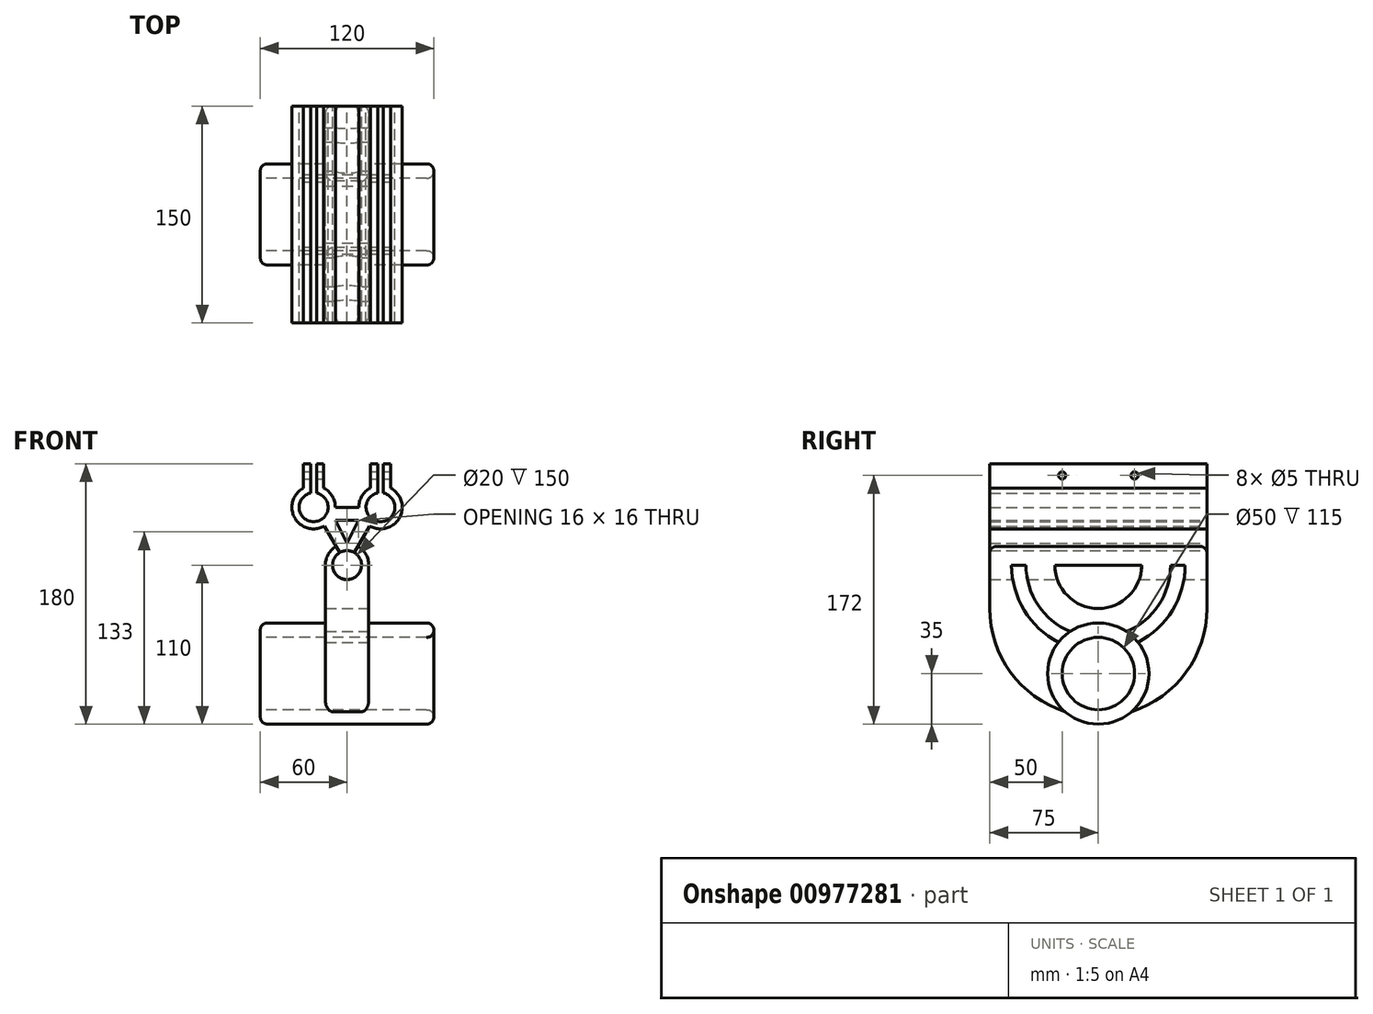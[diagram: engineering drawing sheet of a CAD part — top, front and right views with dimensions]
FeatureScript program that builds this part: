
annotation { "Feature Type Name" : "Feature", "Feature Type Description" : "" }
export const myFeature = defineFeature(function(context is Context, id is Id, definition is map)
    precondition{}
    {
        {
            var Q0;
            Q0=qCreatedBy(makeId("Front.planeOp"),FACE);
            var sketch = newSketch(context, id + "F0", { "sketchPlane" : qUnion([Q0])});
            skCircle(sketch, "E0", {"center": v(0, 0) * mm, "radius": 10 * mm});
            skCircle(sketch, "E1", {"center": v(23.1, 40) * mm, "radius": 10 * mm});
            skCircle(sketch, "E2", {"center": v(-23.1, 40) * mm, "radius": 10 * mm});
            skCircle(sketch, "E3", {"center": v(-23.1, 40) * mm, "radius": 15 * mm});
            skCircle(sketch, "E4", {"center": v(23.1, 40) * mm, "radius": 15 * mm});
            skCircle(sketch, "E5", {"center": v(0, 0) * mm, "radius": 15 * mm});
            skLineSegment(sketch, "E6", {"start": v(0, 0) * mm, "end": v(-23.1, 40) * mm});
            skLineSegment(sketch, "E7", {"start": v(23.1, 40) * mm, "end": v(0, 0) * mm});
            skLineSegment(sketch, "E8", {"start": v(-23.1, 40) * mm, "end": v(23.1, 40) * mm});
            skLineSegment(sketch, "E9.bottom", {"start": v(-2.5, 0) * mm, "end": v(2.5, 0) * mm});
            skLineSegment(sketch, "E9.top", {"start": v(-2.5, -30) * mm, "end": v(2.5, -30) * mm});
            skLineSegment(sketch, "E9.left", {"start": v(-2.5, 0) * mm, "end": v(-2.5, -30) * mm});
            skLineSegment(sketch, "E9.right", {"start": v(2.5, 0) * mm, "end": v(2.5, -30) * mm});
            skPoint(sketch, "E9.middle", {"position": v(0, -15) * mm});
            skLineSegment(sketch, "E10.bottom", {"start": v(15, -30) * mm, "end": v(-15, -30) * mm});
            skLineSegment(sketch, "E10.top", {"start": v(15, 0) * mm, "end": v(-15, 0) * mm});
            skLineSegment(sketch, "E10.left", {"start": v(15, -30) * mm, "end": v(15, 0) * mm});
            skLineSegment(sketch, "E10.right", {"start": v(-15, -30) * mm, "end": v(-15, 0) * mm});
            skPoint(sketch, "E11.middle", {"position": v(0, 40) * mm});
            skLineSegment(sketch, "E12.bottom", {"start": v(30.1, 70) * mm, "end": v(16.1, 70) * mm});
            skLineSegment(sketch, "E12.top", {"start": v(30.1, 40) * mm, "end": v(16.1, 40) * mm});
            skLineSegment(sketch, "E12.left", {"start": v(30.1, 70) * mm, "end": v(30.1, 40) * mm});
            skLineSegment(sketch, "E12.right", {"start": v(16.1, 70) * mm, "end": v(16.1, 40) * mm});
            skPoint(sketch, "E12.middle", {"position": v(23.1, 55) * mm});
            skLineSegment(sketch, "E13.bottom", {"start": v(-16.1, 70) * mm, "end": v(-30.1, 70) * mm});
            skLineSegment(sketch, "E13.top", {"start": v(-16.1, 40) * mm, "end": v(-30.1, 40) * mm});
            skLineSegment(sketch, "E13.left", {"start": v(-16.1, 70) * mm, "end": v(-16.1, 40) * mm});
            skLineSegment(sketch, "E13.right", {"start": v(-30.1, 70) * mm, "end": v(-30.1, 40) * mm});
            skPoint(sketch, "E13.middle", {"position": v(-23.1, 55) * mm});
            skLineSegment(sketch, "E14.bottom", {"start": v(-25.1, 70) * mm, "end": v(-21.1, 70) * mm});
            skLineSegment(sketch, "E14.top", {"start": v(-25.1, 40) * mm, "end": v(-21.1, 40) * mm});
            skLineSegment(sketch, "E14.left", {"start": v(-25.1, 70) * mm, "end": v(-25.1, 40) * mm});
            skLineSegment(sketch, "E14.right", {"start": v(-21.1, 70) * mm, "end": v(-21.1, 40) * mm});
            skLineSegment(sketch, "E15.bottom", {"start": v(21.1, 70) * mm, "end": v(25.1, 70) * mm});
            skLineSegment(sketch, "E15.top", {"start": v(21.1, 40) * mm, "end": v(25.1, 40) * mm});
            skLineSegment(sketch, "E15.left", {"start": v(21.1, 70) * mm, "end": v(21.1, 40) * mm});
            skLineSegment(sketch, "E15.right", {"start": v(25.1, 70) * mm, "end": v(25.1, 40) * mm});
            skSolve(sketch);
        }
        {
            var Q0;
            {var subQ0=sQuery(id+"F0.wireOp",EDGE,"E13.left");var subQ1=sQuery(id+"F0.wireOp",EDGE,"E3");var subQ2=makeQuery(id+"F0.imprint","INTERSECT",VERTEX,{"derivedFrom":[subQ1,subQ0]});Q0=makeQuery(id+"F0.imprint","IMPRINT",FACE,{"disambiguationData":[TD([[makeQuery(id+"F0.imprint","IMPRINT",EDGE,{"disambiguationData":[TD([[subQ2,-1.0]])],"derivedFrom":subQ1}),-1.0]])]});}
            var Q1;
            {var subQ0=sQuery(id+"F0.wireOp",EDGE,"E13.right");var subQ1=sQuery(id+"F0.wireOp",EDGE,"E3");var subQ2=makeQuery(id+"F0.imprint","INTERSECT",VERTEX,{"derivedFrom":[subQ1,subQ0]});Q1=makeQuery(id+"F0.imprint","IMPRINT",FACE,{"disambiguationData":[TD([[makeQuery(id+"F0.imprint","IMPRINT",EDGE,{"disambiguationData":[TD([[subQ2,1.0]])],"derivedFrom":subQ1}),-1.0]])]});}
            var Q2;
            {var subQ0=sQuery(id+"F0.wireOp",EDGE,"E12.left");var subQ1=sQuery(id+"F0.wireOp",EDGE,"E4");var subQ2=makeQuery(id+"F0.imprint","INTERSECT",VERTEX,{"derivedFrom":[subQ1,subQ0]});Q2=makeQuery(id+"F0.imprint","IMPRINT",FACE,{"disambiguationData":[TD([[makeQuery(id+"F0.imprint","IMPRINT",EDGE,{"disambiguationData":[TD([[subQ2,-1.0]])],"derivedFrom":subQ1}),-1.0]])]});}
            var Q3;
            {var subQ0=sQuery(id+"F0.wireOp",EDGE,"E12.right");var subQ1=sQuery(id+"F0.wireOp",EDGE,"E4");var subQ2=makeQuery(id+"F0.imprint","INTERSECT",VERTEX,{"derivedFrom":[subQ1,subQ0]});Q3=makeQuery(id+"F0.imprint","IMPRINT",FACE,{"disambiguationData":[TD([[makeQuery(id+"F0.imprint","IMPRINT",EDGE,{"disambiguationData":[TD([[subQ2,1.0]])],"derivedFrom":subQ1}),-1.0]])]});}
            var Q4;
            {var subQ0=sQuery(id+"F0.wireOp",EDGE,"E10.right");var subQ1=sQuery(id+"F0.wireOp",EDGE,"E5");var subQ2=makeQuery(id+"F0.imprint","INTERSECT",VERTEX,{"derivedFrom":[subQ1,subQ0]});Q4=makeQuery(id+"F0.imprint","IMPRINT",FACE,{"disambiguationData":[TD([[makeQuery(id+"F0.imprint","IMPRINT",EDGE,{"disambiguationData":[TD([[subQ2,-1.0]])],"derivedFrom":subQ1}),-1.0]])]});}
            var Q5;
            {var subQ0=sQuery(id+"F0.wireOp",EDGE,"E10.left");var subQ1=sQuery(id+"F0.wireOp",EDGE,"E5");var subQ2=makeQuery(id+"F0.imprint","INTERSECT",VERTEX,{"derivedFrom":[subQ1,subQ0]});Q5=makeQuery(id+"F0.imprint","IMPRINT",FACE,{"disambiguationData":[TD([[makeQuery(id+"F0.imprint","IMPRINT",EDGE,{"disambiguationData":[TD([[subQ2,1.0]])],"derivedFrom":subQ1}),-1.0]])]});}
            var Q6;
            {var subQ0=sQuery(id+"F0.wireOp",EDGE,"E6");var subQ1=sQuery(id+"F0.wireOp",EDGE,"E0");var subQ2=makeQuery(id+"F0.imprint","INTERSECT",VERTEX,{"derivedFrom":[subQ1,subQ0]});Q6=makeQuery(id+"F0.imprint","IMPRINT",FACE,{"disambiguationData":[TD([[makeQuery(id+"F0.imprint","IMPRINT",EDGE,{"disambiguationData":[TD([[subQ2,-1.0]])],"derivedFrom":subQ1}),-1.0]])]});}
            var Q7;
            {var subQ0=sQuery(id+"F0.wireOp",EDGE,"E7");var subQ1=sQuery(id+"F0.wireOp",EDGE,"E0");var subQ2=makeQuery(id+"F0.imprint","INTERSECT",VERTEX,{"derivedFrom":[subQ1,subQ0]});Q7=makeQuery(id+"F0.imprint","IMPRINT",FACE,{"disambiguationData":[TD([[makeQuery(id+"F0.imprint","IMPRINT",EDGE,{"disambiguationData":[TD([[subQ2,1.0]])],"derivedFrom":subQ1}),-1.0]])]});}
            var Q8;
            {var subQ0=sQuery(id+"F0.wireOp",EDGE,"E12.right");var subQ1=sQuery(id+"F0.wireOp",EDGE,"E1");var subQ2=makeQuery(id+"F0.imprint","INTERSECT",VERTEX,{"derivedFrom":[subQ1,subQ0]});Q8=makeQuery(id+"F0.imprint","IMPRINT",FACE,{"disambiguationData":[TD([[makeQuery(id+"F0.imprint","IMPRINT",EDGE,{"disambiguationData":[TD([[subQ2,-1.0]])],"derivedFrom":subQ1}),-1.0]])]});}
            var Q9;
            {var subQ0=sQuery(id+"F0.wireOp",EDGE,"E12.left");var subQ1=sQuery(id+"F0.wireOp",EDGE,"E1");var subQ2=makeQuery(id+"F0.imprint","INTERSECT",VERTEX,{"derivedFrom":[subQ1,subQ0]});Q9=makeQuery(id+"F0.imprint","IMPRINT",FACE,{"disambiguationData":[TD([[makeQuery(id+"F0.imprint","IMPRINT",EDGE,{"disambiguationData":[TD([[subQ2,1.0]])],"derivedFrom":subQ1}),-1.0]])]});}
            var Q10;
            {var subQ0=sQuery(id+"F0.wireOp",EDGE,"E13.left");var subQ1=sQuery(id+"F0.wireOp",EDGE,"E2");var subQ2=makeQuery(id+"F0.imprint","INTERSECT",VERTEX,{"derivedFrom":[subQ1,subQ0]});Q10=makeQuery(id+"F0.imprint","IMPRINT",FACE,{"disambiguationData":[TD([[makeQuery(id+"F0.imprint","IMPRINT",EDGE,{"disambiguationData":[TD([[subQ2,1.0]])],"derivedFrom":subQ1}),-1.0]])]});}
            var Q11;
            {var subQ0=sQuery(id+"F0.wireOp",EDGE,"E13.right");var subQ1=sQuery(id+"F0.wireOp",EDGE,"E2");var subQ2=makeQuery(id+"F0.imprint","INTERSECT",VERTEX,{"derivedFrom":[subQ1,subQ0]});Q11=makeQuery(id+"F0.imprint","IMPRINT",FACE,{"disambiguationData":[TD([[makeQuery(id+"F0.imprint","IMPRINT",EDGE,{"disambiguationData":[TD([[subQ2,-1.0]])],"derivedFrom":subQ1}),-1.0]])]});}
            var Q12;
            {var subQ5=sQuery(id+"F0.wireOp",EDGE,"E3");var subQ7=sQuery(id+"F0.wireOp",EDGE,"E8");var subQ11=makeQuery(id+"F0.imprint","INTERSECT",VERTEX,{"derivedFrom":[subQ5,subQ7]});Q12=makeQuery(id+"F0.imprint","IMPRINT",FACE,{"disambiguationData":[TD([[makeQuery(id+"F0.imprint","IMPRINT",EDGE,{"disambiguationData":[TD([[subQ11,1.0]])],"derivedFrom":subQ5}),-1.0]])]});}
            var Q13;
            {var subQ0=sQuery(id+"F0.wireOp",EDGE,"E9.left");var subQ1=sQuery(id+"F0.wireOp",EDGE,"E5");var subQ2=makeQuery(id+"F0.imprint","INTERSECT",VERTEX,{"derivedFrom":[subQ1,subQ0]});Q13=makeQuery(id+"F0.imprint","IMPRINT",FACE,{"disambiguationData":[TD([[makeQuery(id+"F0.imprint","IMPRINT",EDGE,{"disambiguationData":[TD([[subQ2,-1.0]])],"derivedFrom":subQ1}),-1.0]])]});}
            var Q14;
            {var subQ0=sQuery(id+"F0.wireOp",EDGE,"E6");var subQ1=sQuery(id+"F0.wireOp",EDGE,"E0");var subQ2=makeQuery(id+"F0.imprint","INTERSECT",VERTEX,{"derivedFrom":[subQ1,subQ0]});Q14=makeQuery(id+"F0.imprint","IMPRINT",FACE,{"disambiguationData":[TD([[makeQuery(id+"F0.imprint","IMPRINT",EDGE,{"disambiguationData":[TD([[subQ2,1.0]])],"derivedFrom":subQ1}),-1.0]])]});}
            var Q15;
            {var subQ0=sQuery(id+"F0.wireOp",EDGE,"E10.right");var subQ1=sQuery(id+"F0.wireOp",EDGE,"E0");var subQ2=makeQuery(id+"F0.imprint","INTERSECT",VERTEX,{"derivedFrom":[subQ1,subQ0]});Q15=makeQuery(id+"F0.imprint","IMPRINT",FACE,{"disambiguationData":[TD([[makeQuery(id+"F0.imprint","IMPRINT",EDGE,{"disambiguationData":[TD([[subQ2,-1.0]])],"derivedFrom":subQ1}),-1.0]])]});}
            var Q16;
            {var subQ0=sQuery(id+"F0.wireOp",EDGE,"E9.right");var subQ1=sQuery(id+"F0.wireOp",EDGE,"E0");var subQ2=makeQuery(id+"F0.imprint","INTERSECT",VERTEX,{"derivedFrom":[subQ1,subQ0]});Q16=makeQuery(id+"F0.imprint","IMPRINT",FACE,{"disambiguationData":[TD([[makeQuery(id+"F0.imprint","IMPRINT",EDGE,{"disambiguationData":[TD([[subQ2,-1.0]])],"derivedFrom":subQ1}),-1.0]])]});}
            var Q17;
            {var subQ0=sQuery(id+"F0.wireOp",EDGE,"E15.right");var subQ1=sQuery(id+"F0.wireOp",EDGE,"E1");var subQ2=makeQuery(id+"F0.imprint","INTERSECT",VERTEX,{"derivedFrom":[subQ1,subQ0]});Q17=makeQuery(id+"F0.imprint","IMPRINT",FACE,{"disambiguationData":[TD([[makeQuery(id+"F0.imprint","IMPRINT",EDGE,{"disambiguationData":[TD([[subQ2,1.0]])],"derivedFrom":subQ1}),-1.0]])]});}
            var Q18;
            {var subQ0=sQuery(id+"F0.wireOp",EDGE,"E15.left");var subQ1=sQuery(id+"F0.wireOp",EDGE,"E1");var subQ2=makeQuery(id+"F0.imprint","INTERSECT",VERTEX,{"derivedFrom":[subQ1,subQ0]});Q18=makeQuery(id+"F0.imprint","IMPRINT",FACE,{"disambiguationData":[TD([[makeQuery(id+"F0.imprint","IMPRINT",EDGE,{"disambiguationData":[TD([[subQ2,-1.0]])],"derivedFrom":subQ1}),-1.0]])]});}
            var Q19;
            {var subQ0=sQuery(id+"F0.wireOp",EDGE,"E8");var subQ1=sQuery(id+"F0.wireOp",EDGE,"E1");var subQ2=makeQuery(id+"F0.imprint","INTERSECT",VERTEX,{"derivedFrom":[subQ1,subQ0]});Q19=makeQuery(id+"F0.imprint","IMPRINT",FACE,{"disambiguationData":[TD([[makeQuery(id+"F0.imprint","IMPRINT",EDGE,{"disambiguationData":[TD([[subQ2,-1.0]])],"derivedFrom":subQ1}),-1.0]])]});}
            var Q20;
            {var subQ0=sQuery(id+"F0.wireOp",EDGE,"E13.left");var subQ1=sQuery(id+"F0.wireOp",EDGE,"E2");var subQ2=makeQuery(id+"F0.imprint","INTERSECT",VERTEX,{"derivedFrom":[subQ1,subQ0]});Q20=makeQuery(id+"F0.imprint","IMPRINT",FACE,{"disambiguationData":[TD([[makeQuery(id+"F0.imprint","IMPRINT",EDGE,{"disambiguationData":[TD([[subQ2,-1.0]])],"derivedFrom":subQ1}),-1.0]])]});}
            var Q21;
            {var subQ0=sQuery(id+"F0.wireOp",EDGE,"E14.left");var subQ1=sQuery(id+"F0.wireOp",EDGE,"E2");var subQ2=makeQuery(id+"F0.imprint","INTERSECT",VERTEX,{"derivedFrom":[subQ1,subQ0]});Q21=makeQuery(id+"F0.imprint","IMPRINT",FACE,{"disambiguationData":[TD([[makeQuery(id+"F0.imprint","IMPRINT",EDGE,{"disambiguationData":[TD([[subQ2,-1.0]])],"derivedFrom":subQ1}),-1.0]])]});}
            var Q22;
            {var subQ0=sQuery(id+"F0.wireOp",EDGE,"E8");var subQ1=sQuery(id+"F0.wireOp",EDGE,"E2");var subQ2=makeQuery(id+"F0.imprint","INTERSECT",VERTEX,{"derivedFrom":[subQ1,subQ0]});Q22=makeQuery(id+"F0.imprint","IMPRINT",FACE,{"disambiguationData":[TD([[makeQuery(id+"F0.imprint","IMPRINT",EDGE,{"disambiguationData":[TD([[subQ2,1.0]])],"derivedFrom":subQ1}),-1.0]])]});}
            var Q23;
            {var subQ0=sQuery(id+"F0.wireOp",EDGE,"E9.left");var subQ1=sQuery(id+"F0.wireOp",EDGE,"E0");var subQ2=makeQuery(id+"F0.imprint","INTERSECT",VERTEX,{"derivedFrom":[subQ1,subQ0]});Q23=makeQuery(id+"F0.imprint","IMPRINT",FACE,{"disambiguationData":[TD([[makeQuery(id+"F0.imprint","IMPRINT",EDGE,{"disambiguationData":[TD([[subQ2,-1.0]])],"derivedFrom":subQ1}),-1.0]])]});}
            extrude(context, id + "F1", {"entities" : qUnion([Q0, Q1, Q2, Q3, Q4, Q5, Q6, Q7, Q8, Q9, Q10, Q11, Q12, Q13, Q14, Q15, Q16, Q17, Q18, Q19, Q20, Q21, Q22, Q23]), "depth" : 150 * mm, "offsetDistance" : 25 * mm});
        }
        {
            var Q0;
            Q0=makeQuery(id+"F1.opExtrude","SWEPT_FACE",FACE,{"disambiguationData":[OSD([sQuery(id+"F0.wireOp",EDGE,"E12.left")])]});
            var sketch = newSketch(context, id + "F2", { "sketchPlane" : qUnion([Q0])});
            skPoint(sketch, "E16.centerSnap0", {"position": v(-150, 61.63) * mm});
            skCircle(sketch, "E17", {"center": v(-100, 62) * mm, "radius": 2.5 * mm});
            skCircle(sketch, "E18", {"center": v(-50, 62) * mm, "radius": 2.5 * mm});
            skSolve(sketch);
        }
        {
            var Q0;
            Q0=qSketchRegion(id+"F2",true);
            extrude(context, id + "F3", {"entities" : qUnion([Q0]), "operationType" : NewBodyOperationType.REMOVE, "oppositeDirection" : true, "depth" : 80 * mm, "offsetDistance" : 25 * mm});
        }
        {
            var Q0;
            Q0=makeQuery(id+"F1.opExtrude","SWEPT_FACE",FACE,{"disambiguationData":[OSD([sQuery(id+"F0.wireOp",EDGE,"E10.right")])]});
            var sketch = newSketch(context, id + "F4", { "sketchPlane" : qUnion([Q0])});
            skArc(sketch, "E19", {"start": v(0, -30) * mm, "mid": v(75, -105) * mm, "end": v(150, -30) * mm});
            skLineSegment(sketch, "E20", {"start": v(150, -30) * mm, "end": v(0, -30) * mm});
            skCircle(sketch, "E21", {"center": v(75, -75) * mm, "radius": 25 * mm});
            skCircle(sketch, "E22", {"center": v(75, -75) * mm, "radius": 35 * mm});
            skSolve(sketch);
        }
        {
            var Q0;
            Q0=makeQuery(id+"F4.imprint","IMPRINT",FACE,{"disambiguationData":[TD([[makeQuery(id+"F4.imprint","IMPRINT",EDGE,{"derivedFrom":sQuery(id+"F4.wireOp",EDGE,"E19")}),1.0]])]});
            var Q1;
            {var subQ0=sQuery(id+"F4.wireOp",EDGE,"err0hHyo-BO9M-5nqk-DgeP-qzasn8KT2656");var subQ1=sQuery(id+"F4.wireOp",EDGE,"WYPfFYgc-KuOW-hBuJ-W0P3-EaMtmuAlXF2T");var subQ2=makeQuery(id+"F4.imprint","INTERSECT",VERTEX,{"derivedFrom":[subQ1,subQ0]});Q1=makeQuery(id+"F4.imprint","IMPRINT",FACE,{"disambiguationData":[TD([[makeQuery(id+"F4.imprint","IMPRINT",EDGE,{"disambiguationData":[TD([[subQ2,-1.0]])],"derivedFrom":subQ1}),1.0]])]});}
            var Q2;
            {var subQ0=sQuery(id+"F4.wireOp",EDGE,"err0hHyo-BO9M-5nqk-DgeP-qzasn8KT2656");var subQ1=sQuery(id+"F4.wireOp",EDGE,"YoelF4l8-Clh2-Jh8U-mLRx-JcdggAHO28kU");var subQ2=makeQuery(id+"F4.imprint","INTERSECT",VERTEX,{"derivedFrom":[subQ1,subQ0]});Q2=makeQuery(id+"F4.imprint","IMPRINT",FACE,{"disambiguationData":[TD([[makeQuery(id+"F4.imprint","IMPRINT",EDGE,{"disambiguationData":[TD([[subQ2,-1.0]])],"derivedFrom":subQ1}),-1.0]])]});}
            var Q3;
            Q3=makeQuery(id+"F4.imprint","IMPRINT",FACE,{"disambiguationData":[TD([[makeQuery(id+"F4.imprint","IMPRINT",EDGE,{"derivedFrom":sQuery(id+"F4.wireOp",EDGE,"U86jdZLp-OsUm-K8QV-z9DL-TqobfUC9Fsd7")}),-1.0]])]});
            var Q4;
            {var subQ3=sQuery(id+"F4.wireOp",EDGE,"E8fOwTEM-Ix1q-ZMXN-z86o-tg2dsx62YHI1");var subQ6=sQuery(id+"F4.wireOp",EDGE,"YoelF4l8-Clh2-Jh8U-mLRx-JcdggAHO28kU");var subQ9=makeQuery(id+"F4.imprint","INTERSECT",VERTEX,{"derivedFrom":[subQ6,subQ3]});Q4=makeQuery(id+"F4.imprint","IMPRINT",FACE,{"disambiguationData":[TD([[makeQuery(id+"F4.imprint","IMPRINT",EDGE,{"disambiguationData":[TD([[subQ9,1.0]])],"derivedFrom":subQ6}),-1.0]])]});}
            var Q5;
            {var subQ0=sQuery(id+"F4.wireOp",EDGE,"qKawDexl-ftiU-q3Ic-dwuG-xXSqS1PNBGBF");var subQ1=sQuery(id+"F4.wireOp",EDGE,"WYPfFYgc-KuOW-hBuJ-W0P3-EaMtmuAlXF2T");var subQ2=makeQuery(id+"F4.imprint","INTERSECT",VERTEX,{"derivedFrom":[subQ1,subQ0]});Q5=makeQuery(id+"F4.imprint","IMPRINT",FACE,{"disambiguationData":[TD([[makeQuery(id+"F4.imprint","IMPRINT",EDGE,{"disambiguationData":[TD([[subQ2,-1.0]])],"derivedFrom":subQ1}),1.0]])]});}
            var Q6;
            Q6=makeQuery(id+"F4.imprint","IMPRINT",FACE,{"disambiguationData":[TD([[makeQuery(id+"F4.imprint","IMPRINT",EDGE,{"derivedFrom":sQuery(id+"F4.wireOp",EDGE,"E21")}),-1.0]])]});
            var Q7;
            {var subQ0=sQuery(id+"F4.wireOp",EDGE,"E22");var subQ1=sQuery(id+"F4.wireOp",EDGE,"E19");var subQ2=makeQuery(id+"F4.imprint","INTERSECT",VERTEX,{"disambiguationData":[OD(0.0)],"derivedFrom":[subQ1,subQ0]});Q7=makeQuery(id+"F4.imprint","IMPRINT",FACE,{"disambiguationData":[TD([[makeQuery(id+"F4.imprint","IMPRINT",EDGE,{"disambiguationData":[TD([[subQ2,-1.0]])],"derivedFrom":subQ1}),-1.0]])]});}
            extrude(context, id + "F5", {"entities" : qUnion([Q0, Q1, Q2, Q3, Q4, Q5, Q6, Q7]), "operationType" : NewBodyOperationType.ADD, "oppositeDirection" : true, "depth" : 30 * mm, "offsetDistance" : 25 * mm});
        }
        {
            var Q0;
            Q0=makeQuery(id+"F4.imprint","IMPRINT",FACE,{"disambiguationData":[TD([[makeQuery(id+"F4.imprint","IMPRINT",EDGE,{"derivedFrom":sQuery(id+"F4.wireOp",EDGE,"E21")}),-1.0]])]});
            var Q1;
            {var subQ0=sQuery(id+"F4.wireOp",EDGE,"E22");var subQ1=sQuery(id+"F4.wireOp",EDGE,"E19");var subQ2=makeQuery(id+"F4.imprint","INTERSECT",VERTEX,{"disambiguationData":[OD(0.0)],"derivedFrom":[subQ1,subQ0]});Q1=makeQuery(id+"F4.imprint","IMPRINT",FACE,{"disambiguationData":[TD([[makeQuery(id+"F4.imprint","IMPRINT",EDGE,{"disambiguationData":[TD([[subQ2,-1.0]])],"derivedFrom":subQ1}),-1.0]])]});}
            extrude(context, id + "F6", {"entities" : qUnion([Q0, Q1]), "operationType" : NewBodyOperationType.ADD, "depth" : 45 * mm, "offsetDistance" : 25 * mm, "hasSecondDirection" : true, "secondDirectionOppositeDirection" : true, "secondDirectionDepth" : 75 * mm});
        }
        {
            var Q0;
            Q0=makeQuery(id+"F5.boolean.opBoolean","MERGE",FACE,{"derivedFrom":[makeQuery(id+"F1.opExtrude","SWEPT_FACE",FACE,{"disambiguationData":[OSD([sQuery(id+"F0.wireOp",EDGE,"E10.left")])]}),makeQuery(id+"F5.opExtrude","CAP_FACE",FACE,{"disambiguationData":[OSD([sQuery(id+"F4.wireOp",EDGE,"E19"),sQuery(id+"F4.wireOp",EDGE,"E20"),sQuery(id+"F4.wireOp",EDGE,"E21")])],"isStart":false})]});
            var sketch = newSketch(context, id + "F7", { "sketchPlane" : qUnion([Q0])});
            skCircle(sketch, "E23", {"center": v(-75, 0) * mm, "radius": 30 * mm});
            skCircle(sketch, "E24", {"center": v(-75, 0) * mm, "radius": 50 * mm});
            skCircle(sketch, "E25", {"center": v(-75, 0) * mm, "radius": 60 * mm});
            skCircle(sketch, "E26", {"center": v(-75, -30) * mm, "radius": 90 * mm});
            skCircle(sketch, "E27", {"center": v(-75, -30) * mm, "radius": 70 * mm});
            skSolve(sketch);
        }
        {
            var Q0;
            {var subQ0=sQuery(id+"F7.wireOp",EDGE,"E23");var subQ1=makeQuery(id+"F1.opExtrude","SWEPT_EDGE",EDGE,{"disambiguationData":[OSD([sQuery(id+"F0.wireOp",EDGE,"E5"),sQuery(id+"F0.wireOp",EDGE,"E10.top"),sQuery(id+"F0.wireOp",EDGE,"E10.left")])]});var subQ2=makeQuery(id+"F7.imprint","INTERSECT",VERTEX,{"disambiguationData":[OD(0.0)],"derivedFrom":[subQ1,subQ0]});Q0=makeQuery(id+"F7.imprint","IMPRINT",FACE,{"disambiguationData":[TD([[makeQuery(id+"F7.imprint","IMPRINT",EDGE,{"disambiguationData":[TD([[subQ2,1.0]])],"derivedFrom":subQ0}),1.0]])]});}
            var Q1;
            {var subQ0=sQuery(id+"F7.wireOp",EDGE,"E24");var subQ1=sQuery(id+"F0.wireOp",EDGE,"E10.left");var subQ2=makeQuery(id+"F1.opExtrude","SWEPT_EDGE",EDGE,{"disambiguationData":[OSD([sQuery(id+"F0.wireOp",EDGE,"E5"),sQuery(id+"F0.wireOp",EDGE,"E10.top"),subQ1])]});var subQ3=makeQuery(id+"F7.imprint","INTERSECT",VERTEX,{"disambiguationData":[OD(1.0)],"derivedFrom":[subQ2,subQ0]});Q1=makeQuery(id+"F7.imprint","IMPRINT",FACE,{"disambiguationData":[TD([[makeQuery(id+"F7.imprint","IMPRINT",EDGE,{"disambiguationData":[TD([[subQ3,1.0]])],"derivedFrom":subQ2}),-1.0]])]});}
            var Q2;
            {var subQ0=sQuery(id+"F7.wireOp",EDGE,"E24");var subQ1=sQuery(id+"F0.wireOp",EDGE,"E10.left");var subQ2=makeQuery(id+"F1.opExtrude","SWEPT_EDGE",EDGE,{"disambiguationData":[OSD([sQuery(id+"F0.wireOp",EDGE,"E5"),sQuery(id+"F0.wireOp",EDGE,"E10.top"),subQ1])]});var subQ3=makeQuery(id+"F7.imprint","INTERSECT",VERTEX,{"disambiguationData":[OD(0.0)],"derivedFrom":[subQ2,subQ0]});Q2=makeQuery(id+"F7.imprint","IMPRINT",FACE,{"disambiguationData":[TD([[makeQuery(id+"F7.imprint","IMPRINT",EDGE,{"disambiguationData":[TD([[subQ3,-1.0]])],"derivedFrom":subQ2}),-1.0]])]});}
            extrude(context, id + "F8", {"entities" : qUnion([Q0, Q1, Q2]), "operationType" : NewBodyOperationType.REMOVE, "oppositeDirection" : true, "depth" : 30 * mm, "offsetDistance" : 25 * mm});
        }
        {
            var Q0;
            {var subQ0=sQuery(id+"F4.wireOp",EDGE,"E19");var subQ1=sQuery(id+"F0.wireOp",EDGE,"E10.left");Q0=makeQuery(id+"F6.boolean.opBoolean","SPLIT",EDGE,{"disambiguationData":[TD([makeQuery(id+"F1.opExtrude","CAP_FACE",FACE,{"disambiguationData":[OSD([sQuery(id+"F0.wireOp",EDGE,"E0"),sQuery(id+"F0.wireOp",EDGE,"E1"),sQuery(id+"F0.wireOp",EDGE,"E2"),sQuery(id+"F0.wireOp",EDGE,"E3"),sQuery(id+"F0.wireOp",EDGE,"E4"),sQuery(id+"F0.wireOp",EDGE,"E5"),sQuery(id+"F0.wireOp",EDGE,"E6"),sQuery(id+"F0.wireOp",EDGE,"E7"),sQuery(id+"F0.wireOp",EDGE,"E8"),sQuery(id+"F0.wireOp",EDGE,"E10.bottom"),subQ1,sQuery(id+"F0.wireOp",EDGE,"E10.right"),sQuery(id+"F0.wireOp",EDGE,"E12.bottom"),sQuery(id+"F0.wireOp",EDGE,"E12.left"),sQuery(id+"F0.wireOp",EDGE,"E12.right"),sQuery(id+"F0.wireOp",EDGE,"E13.bottom"),sQuery(id+"F0.wireOp",EDGE,"E13.left"),sQuery(id+"F0.wireOp",EDGE,"E13.right"),sQuery(id+"F0.wireOp",EDGE,"E14.left"),sQuery(id+"F0.wireOp",EDGE,"E14.right"),sQuery(id+"F0.wireOp",EDGE,"E15.left"),sQuery(id+"F0.wireOp",EDGE,"E15.right")])],"isStart":true})])],"derivedFrom":makeQuery(id+"F5.opExtrude","CAP_EDGE",EDGE,{"disambiguationData":[OSD([subQ0])],"isStart":false})});}
            var Q1;
            {var subQ0=sQuery(id+"F7.wireOp",EDGE,"E26");var subQ1=makeQuery(id+"F7.imprint","INTERSECT",VERTEX,{"disambiguationData":[OD(1.0)],"derivedFrom":[sQuery(id+"F7.wireOp",EDGE,"E25"),subQ0]});Q1=makeQuery(id+"F8.boolean.opBoolean","COPY",EDGE,{"derivedFrom":makeQuery(id+"F8.opExtrude","CAP_EDGE",EDGE,{"disambiguationData":[OSD([subQ0]),TDD([makeQuery(id+"F7.imprint","IMPRINT",EDGE,{"disambiguationData":[TD([[subQ1,-1.0]])],"derivedFrom":subQ0}),makeQuery(id+"F7.imprint","IMPRINT",EDGE,{"disambiguationData":[TD([[subQ1,1.0]])],"derivedFrom":subQ0})])],"isStart":true})});}
            var Q2;
            {var subQ0=sQuery(id+"F7.wireOp",EDGE,"E24");var subQ1=makeQuery(id+"F7.imprint","INTERSECT",VERTEX,{"disambiguationData":[OD(1.0)],"derivedFrom":[subQ0,sQuery(id+"F7.wireOp",EDGE,"E27")]});Q2=makeQuery(id+"F8.boolean.opBoolean","COPY",EDGE,{"derivedFrom":makeQuery(id+"F8.opExtrude","CAP_EDGE",EDGE,{"disambiguationData":[OSD([subQ0]),TDD([makeQuery(id+"F7.imprint","IMPRINT",EDGE,{"disambiguationData":[TD([[subQ1,1.0]])],"derivedFrom":subQ0}),makeQuery(id+"F7.imprint","IMPRINT",EDGE,{"disambiguationData":[TD([[subQ1,-1.0]])],"derivedFrom":subQ0})])],"isStart":true})});}
            var Q3;
            Q3=makeQuery(id+"F8.boolean.opBoolean","COPY",EDGE,{"derivedFrom":makeQuery(id+"F8.opExtrude","CAP_EDGE",EDGE,{"disambiguationData":[OSD([sQuery(id+"F7.wireOp",EDGE,"E23")])],"isStart":true})});
            var Q4;
            {var subQ0=sQuery(id+"F7.wireOp",EDGE,"E24");var subQ1=makeQuery(id+"F7.imprint","INTERSECT",VERTEX,{"disambiguationData":[OD(0.0)],"derivedFrom":[subQ0,sQuery(id+"F7.wireOp",EDGE,"E27")]});Q4=makeQuery(id+"F8.boolean.opBoolean","COPY",EDGE,{"derivedFrom":makeQuery(id+"F8.opExtrude","CAP_EDGE",EDGE,{"disambiguationData":[OSD([subQ0]),TDD([makeQuery(id+"F7.imprint","IMPRINT",EDGE,{"disambiguationData":[TD([[subQ1,1.0]])],"derivedFrom":subQ0}),makeQuery(id+"F7.imprint","IMPRINT",EDGE,{"disambiguationData":[TD([[subQ1,-1.0]])],"derivedFrom":subQ0})])],"isStart":true})});}
            var Q5;
            {var subQ0=sQuery(id+"F7.wireOp",EDGE,"E26");var subQ1=makeQuery(id+"F7.imprint","INTERSECT",VERTEX,{"disambiguationData":[OD(0.0)],"derivedFrom":[sQuery(id+"F7.wireOp",EDGE,"E25"),subQ0]});Q5=makeQuery(id+"F8.boolean.opBoolean","COPY",EDGE,{"derivedFrom":makeQuery(id+"F8.opExtrude","CAP_EDGE",EDGE,{"disambiguationData":[OSD([subQ0]),TDD([makeQuery(id+"F7.imprint","IMPRINT",EDGE,{"disambiguationData":[TD([[subQ1,1.0]])],"derivedFrom":subQ0}),makeQuery(id+"F7.imprint","IMPRINT",EDGE,{"disambiguationData":[TD([[subQ1,-1.0]])],"derivedFrom":subQ0})])],"isStart":true})});}
            var Q6;
            {var subQ0=sQuery(id+"F4.wireOp",EDGE,"E19");var subQ1=sQuery(id+"F0.wireOp",EDGE,"E10.left");Q6=makeQuery(id+"F6.boolean.opBoolean","SPLIT",EDGE,{"disambiguationData":[TD([makeQuery(id+"F1.opExtrude","CAP_FACE",FACE,{"disambiguationData":[OSD([sQuery(id+"F0.wireOp",EDGE,"E0"),sQuery(id+"F0.wireOp",EDGE,"E1"),sQuery(id+"F0.wireOp",EDGE,"E2"),sQuery(id+"F0.wireOp",EDGE,"E3"),sQuery(id+"F0.wireOp",EDGE,"E4"),sQuery(id+"F0.wireOp",EDGE,"E5"),sQuery(id+"F0.wireOp",EDGE,"E6"),sQuery(id+"F0.wireOp",EDGE,"E7"),sQuery(id+"F0.wireOp",EDGE,"E8"),sQuery(id+"F0.wireOp",EDGE,"E10.bottom"),subQ1,sQuery(id+"F0.wireOp",EDGE,"E10.right"),sQuery(id+"F0.wireOp",EDGE,"E12.bottom"),sQuery(id+"F0.wireOp",EDGE,"E12.left"),sQuery(id+"F0.wireOp",EDGE,"E12.right"),sQuery(id+"F0.wireOp",EDGE,"E13.bottom"),sQuery(id+"F0.wireOp",EDGE,"E13.left"),sQuery(id+"F0.wireOp",EDGE,"E13.right"),sQuery(id+"F0.wireOp",EDGE,"E14.left"),sQuery(id+"F0.wireOp",EDGE,"E14.right"),sQuery(id+"F0.wireOp",EDGE,"E15.left"),sQuery(id+"F0.wireOp",EDGE,"E15.right")])],"isStart":false})])],"derivedFrom":makeQuery(id+"F5.opExtrude","CAP_EDGE",EDGE,{"disambiguationData":[OSD([subQ0])],"isStart":false})});}
            var Q7;
            {var subQ0=sQuery(id+"F4.wireOp",EDGE,"E19");var subQ1=sQuery(id+"F0.wireOp",EDGE,"E10.right");Q7=makeQuery(id+"F6.boolean.opBoolean","SPLIT",EDGE,{"disambiguationData":[TD([makeQuery(id+"F1.opExtrude","CAP_FACE",FACE,{"disambiguationData":[OSD([sQuery(id+"F0.wireOp",EDGE,"E0"),sQuery(id+"F0.wireOp",EDGE,"E1"),sQuery(id+"F0.wireOp",EDGE,"E2"),sQuery(id+"F0.wireOp",EDGE,"E3"),sQuery(id+"F0.wireOp",EDGE,"E4"),sQuery(id+"F0.wireOp",EDGE,"E5"),sQuery(id+"F0.wireOp",EDGE,"E6"),sQuery(id+"F0.wireOp",EDGE,"E7"),sQuery(id+"F0.wireOp",EDGE,"E8"),sQuery(id+"F0.wireOp",EDGE,"E10.bottom"),sQuery(id+"F0.wireOp",EDGE,"E10.left"),subQ1,sQuery(id+"F0.wireOp",EDGE,"E12.bottom"),sQuery(id+"F0.wireOp",EDGE,"E12.left"),sQuery(id+"F0.wireOp",EDGE,"E12.right"),sQuery(id+"F0.wireOp",EDGE,"E13.bottom"),sQuery(id+"F0.wireOp",EDGE,"E13.left"),sQuery(id+"F0.wireOp",EDGE,"E13.right"),sQuery(id+"F0.wireOp",EDGE,"E14.left"),sQuery(id+"F0.wireOp",EDGE,"E14.right"),sQuery(id+"F0.wireOp",EDGE,"E15.left"),sQuery(id+"F0.wireOp",EDGE,"E15.right")])],"isStart":false})])],"derivedFrom":makeQuery(id+"F5.opExtrude","CAP_EDGE",EDGE,{"disambiguationData":[OSD([subQ0])],"isStart":true})});}
            var Q8;
            {var subQ0=sQuery(id+"F4.wireOp",EDGE,"E19");var subQ1=sQuery(id+"F0.wireOp",EDGE,"E10.right");Q8=makeQuery(id+"F6.boolean.opBoolean","SPLIT",EDGE,{"disambiguationData":[TD([makeQuery(id+"F1.opExtrude","CAP_FACE",FACE,{"disambiguationData":[OSD([sQuery(id+"F0.wireOp",EDGE,"E0"),sQuery(id+"F0.wireOp",EDGE,"E1"),sQuery(id+"F0.wireOp",EDGE,"E2"),sQuery(id+"F0.wireOp",EDGE,"E3"),sQuery(id+"F0.wireOp",EDGE,"E4"),sQuery(id+"F0.wireOp",EDGE,"E5"),sQuery(id+"F0.wireOp",EDGE,"E6"),sQuery(id+"F0.wireOp",EDGE,"E7"),sQuery(id+"F0.wireOp",EDGE,"E8"),sQuery(id+"F0.wireOp",EDGE,"E10.bottom"),sQuery(id+"F0.wireOp",EDGE,"E10.left"),subQ1,sQuery(id+"F0.wireOp",EDGE,"E12.bottom"),sQuery(id+"F0.wireOp",EDGE,"E12.left"),sQuery(id+"F0.wireOp",EDGE,"E12.right"),sQuery(id+"F0.wireOp",EDGE,"E13.bottom"),sQuery(id+"F0.wireOp",EDGE,"E13.left"),sQuery(id+"F0.wireOp",EDGE,"E13.right"),sQuery(id+"F0.wireOp",EDGE,"E14.left"),sQuery(id+"F0.wireOp",EDGE,"E14.right"),sQuery(id+"F0.wireOp",EDGE,"E15.left"),sQuery(id+"F0.wireOp",EDGE,"E15.right")])],"isStart":true})])],"derivedFrom":makeQuery(id+"F5.opExtrude","CAP_EDGE",EDGE,{"disambiguationData":[OSD([subQ0])],"isStart":true})});}
            var Q9;
            {var subQ0=sQuery(id+"F7.wireOp",EDGE,"E26");var subQ1=makeQuery(id+"F7.imprint","INTERSECT",VERTEX,{"disambiguationData":[OD(1.0)],"derivedFrom":[sQuery(id+"F7.wireOp",EDGE,"E25"),subQ0]});Q9=makeQuery(id+"F8.boolean.opBoolean","COPY",EDGE,{"derivedFrom":makeQuery(id+"F8.opExtrude","CAP_EDGE",EDGE,{"disambiguationData":[OSD([subQ0]),TDD([makeQuery(id+"F7.imprint","IMPRINT",EDGE,{"disambiguationData":[TD([[subQ1,-1.0]])],"derivedFrom":subQ0}),makeQuery(id+"F7.imprint","IMPRINT",EDGE,{"disambiguationData":[TD([[subQ1,1.0]])],"derivedFrom":subQ0})])],"isStart":false})});}
            var Q10;
            {var subQ0=sQuery(id+"F7.wireOp",EDGE,"E24");var subQ1=makeQuery(id+"F7.imprint","INTERSECT",VERTEX,{"disambiguationData":[OD(1.0)],"derivedFrom":[subQ0,sQuery(id+"F7.wireOp",EDGE,"E27")]});Q10=makeQuery(id+"F8.boolean.opBoolean","COPY",EDGE,{"derivedFrom":makeQuery(id+"F8.opExtrude","CAP_EDGE",EDGE,{"disambiguationData":[OSD([subQ0]),TDD([makeQuery(id+"F7.imprint","IMPRINT",EDGE,{"disambiguationData":[TD([[subQ1,1.0]])],"derivedFrom":subQ0}),makeQuery(id+"F7.imprint","IMPRINT",EDGE,{"disambiguationData":[TD([[subQ1,-1.0]])],"derivedFrom":subQ0})])],"isStart":false})});}
            var Q11;
            Q11=makeQuery(id+"F8.boolean.opBoolean","COPY",EDGE,{"derivedFrom":makeQuery(id+"F8.opExtrude","CAP_EDGE",EDGE,{"disambiguationData":[OSD([sQuery(id+"F7.wireOp",EDGE,"E23")])],"isStart":false})});
            var Q12;
            {var subQ0=sQuery(id+"F7.wireOp",EDGE,"E24");var subQ1=makeQuery(id+"F7.imprint","INTERSECT",VERTEX,{"disambiguationData":[OD(0.0)],"derivedFrom":[subQ0,sQuery(id+"F7.wireOp",EDGE,"E27")]});Q12=makeQuery(id+"F8.boolean.opBoolean","COPY",EDGE,{"derivedFrom":makeQuery(id+"F8.opExtrude","CAP_EDGE",EDGE,{"disambiguationData":[OSD([subQ0]),TDD([makeQuery(id+"F7.imprint","IMPRINT",EDGE,{"disambiguationData":[TD([[subQ1,1.0]])],"derivedFrom":subQ0}),makeQuery(id+"F7.imprint","IMPRINT",EDGE,{"disambiguationData":[TD([[subQ1,-1.0]])],"derivedFrom":subQ0})])],"isStart":false})});}
            var Q13;
            {var subQ0=sQuery(id+"F7.wireOp",EDGE,"E26");var subQ1=makeQuery(id+"F7.imprint","INTERSECT",VERTEX,{"disambiguationData":[OD(0.0)],"derivedFrom":[sQuery(id+"F7.wireOp",EDGE,"E25"),subQ0]});Q13=makeQuery(id+"F8.boolean.opBoolean","COPY",EDGE,{"derivedFrom":makeQuery(id+"F8.opExtrude","CAP_EDGE",EDGE,{"disambiguationData":[OSD([subQ0]),TDD([makeQuery(id+"F7.imprint","IMPRINT",EDGE,{"disambiguationData":[TD([[subQ1,1.0]])],"derivedFrom":subQ0}),makeQuery(id+"F7.imprint","IMPRINT",EDGE,{"disambiguationData":[TD([[subQ1,-1.0]])],"derivedFrom":subQ0})])],"isStart":false})});}
            var Q14;
            {var subQ0=sQuery(id+"F7.wireOp",EDGE,"E24");var subQ1=sQuery(id+"F0.wireOp",EDGE,"E10.left");Q14=makeQuery(id+"F8.boolean.opBoolean","COPY",EDGE,{"derivedFrom":makeQuery(id+"F8.opExtrude","CAP_EDGE",EDGE,{"disambiguationData":[OSD([subQ0]),TDD([makeQuery(id+"F7.imprint","IMPRINT",EDGE,{"disambiguationData":[TD([[makeQuery(id+"F7.imprint","INTERSECT",VERTEX,{"disambiguationData":[OD(0.0)],"derivedFrom":[makeQuery(id+"F1.opExtrude","SWEPT_EDGE",EDGE,{"disambiguationData":[OSD([sQuery(id+"F0.wireOp",EDGE,"E5"),sQuery(id+"F0.wireOp",EDGE,"E10.top"),subQ1])]}),subQ0]}),1.0]])],"derivedFrom":subQ0})])],"isStart":true})});}
            var Q15;
            {var subQ0=sQuery(id+"F7.wireOp",EDGE,"E24");var subQ1=sQuery(id+"F0.wireOp",EDGE,"E10.left");Q15=makeQuery(id+"F8.boolean.opBoolean","COPY",EDGE,{"derivedFrom":makeQuery(id+"F8.opExtrude","CAP_EDGE",EDGE,{"disambiguationData":[OSD([subQ0]),TDD([makeQuery(id+"F7.imprint","IMPRINT",EDGE,{"disambiguationData":[TD([[makeQuery(id+"F7.imprint","INTERSECT",VERTEX,{"disambiguationData":[OD(1.0)],"derivedFrom":[makeQuery(id+"F1.opExtrude","SWEPT_EDGE",EDGE,{"disambiguationData":[OSD([sQuery(id+"F0.wireOp",EDGE,"E5"),sQuery(id+"F0.wireOp",EDGE,"E10.top"),subQ1])]}),subQ0]}),-1.0]])],"derivedFrom":subQ0})])],"isStart":true})});}
            var Q16;
            {var subQ0=sQuery(id+"F7.wireOp",EDGE,"E24");var subQ1=sQuery(id+"F0.wireOp",EDGE,"E10.left");Q16=makeQuery(id+"F8.boolean.opBoolean","COPY",EDGE,{"derivedFrom":makeQuery(id+"F8.opExtrude","CAP_EDGE",EDGE,{"disambiguationData":[OSD([subQ0]),TDD([makeQuery(id+"F7.imprint","IMPRINT",EDGE,{"disambiguationData":[TD([[makeQuery(id+"F7.imprint","INTERSECT",VERTEX,{"disambiguationData":[OD(1.0)],"derivedFrom":[makeQuery(id+"F1.opExtrude","SWEPT_EDGE",EDGE,{"disambiguationData":[OSD([sQuery(id+"F0.wireOp",EDGE,"E5"),sQuery(id+"F0.wireOp",EDGE,"E10.top"),subQ1])]}),subQ0]}),-1.0]])],"derivedFrom":subQ0})])],"isStart":false})});}
            var Q17;
            {var subQ0=sQuery(id+"F7.wireOp",EDGE,"E24");var subQ1=sQuery(id+"F0.wireOp",EDGE,"E10.left");Q17=makeQuery(id+"F8.boolean.opBoolean","COPY",EDGE,{"derivedFrom":makeQuery(id+"F8.opExtrude","CAP_EDGE",EDGE,{"disambiguationData":[OSD([subQ0]),TDD([makeQuery(id+"F7.imprint","IMPRINT",EDGE,{"disambiguationData":[TD([[makeQuery(id+"F7.imprint","INTERSECT",VERTEX,{"disambiguationData":[OD(0.0)],"derivedFrom":[makeQuery(id+"F1.opExtrude","SWEPT_EDGE",EDGE,{"disambiguationData":[OSD([sQuery(id+"F0.wireOp",EDGE,"E5"),sQuery(id+"F0.wireOp",EDGE,"E10.top"),subQ1])]}),subQ0]}),1.0]])],"derivedFrom":subQ0})])],"isStart":false})});}
            var Q18;
            {var subQ0=sQuery(id+"F7.wireOp",EDGE,"E25");var subQ1=sQuery(id+"F0.wireOp",EDGE,"E10.left");Q18=makeQuery(id+"F8.boolean.opBoolean","COPY",EDGE,{"derivedFrom":makeQuery(id+"F8.opExtrude","CAP_EDGE",EDGE,{"disambiguationData":[OSD([subQ0]),TDD([makeQuery(id+"F7.imprint","IMPRINT",EDGE,{"disambiguationData":[TD([[makeQuery(id+"F7.imprint","INTERSECT",VERTEX,{"disambiguationData":[OD(0.0)],"derivedFrom":[makeQuery(id+"F1.opExtrude","SWEPT_EDGE",EDGE,{"disambiguationData":[OSD([sQuery(id+"F0.wireOp",EDGE,"E5"),sQuery(id+"F0.wireOp",EDGE,"E10.top"),subQ1])]}),subQ0]}),1.0]])],"derivedFrom":subQ0})])],"isStart":false})});}
            var Q19;
            {var subQ0=sQuery(id+"F7.wireOp",EDGE,"E25");var subQ1=sQuery(id+"F0.wireOp",EDGE,"E10.left");Q19=makeQuery(id+"F8.boolean.opBoolean","COPY",EDGE,{"derivedFrom":makeQuery(id+"F8.opExtrude","CAP_EDGE",EDGE,{"disambiguationData":[OSD([subQ0]),TDD([makeQuery(id+"F7.imprint","IMPRINT",EDGE,{"disambiguationData":[TD([[makeQuery(id+"F7.imprint","INTERSECT",VERTEX,{"disambiguationData":[OD(1.0)],"derivedFrom":[makeQuery(id+"F1.opExtrude","SWEPT_EDGE",EDGE,{"disambiguationData":[OSD([sQuery(id+"F0.wireOp",EDGE,"E5"),sQuery(id+"F0.wireOp",EDGE,"E10.top"),subQ1])]}),subQ0]}),-1.0]])],"derivedFrom":subQ0})])],"isStart":false})});}
            var Q20;
            {var subQ0=sQuery(id+"F7.wireOp",EDGE,"E25");var subQ1=sQuery(id+"F0.wireOp",EDGE,"E10.left");Q20=makeQuery(id+"F8.boolean.opBoolean","COPY",EDGE,{"derivedFrom":makeQuery(id+"F8.opExtrude","CAP_EDGE",EDGE,{"disambiguationData":[OSD([subQ0]),TDD([makeQuery(id+"F7.imprint","IMPRINT",EDGE,{"disambiguationData":[TD([[makeQuery(id+"F7.imprint","INTERSECT",VERTEX,{"disambiguationData":[OD(1.0)],"derivedFrom":[makeQuery(id+"F1.opExtrude","SWEPT_EDGE",EDGE,{"disambiguationData":[OSD([sQuery(id+"F0.wireOp",EDGE,"E5"),sQuery(id+"F0.wireOp",EDGE,"E10.top"),subQ1])]}),subQ0]}),-1.0]])],"derivedFrom":subQ0})])],"isStart":true})});}
            fillet(context, id + "F9", {"entities" : qUnion([Q0, Q1, Q2, Q3, Q4, Q5, Q6, Q7, Q8, Q9, Q10, Q11, Q12, Q13, Q14, Q15, Q16, Q17, Q18, Q19, Q20]), "radius" : 5 * mm, "tangentPropagation" : true, "allowEdgeOverflow" : false});
        }
        {
            var Q0;
            Q0=makeQuery(id+"F6.opExtrude","CAP_EDGE",EDGE,{"disambiguationData":[OSD([sQuery(id+"F4.wireOp",EDGE,"E19")])],"isStart":true});
            var Q1;
            {var subQ0=sQuery(id+"F4.wireOp",EDGE,"E19");var subQ2=sQuery(id+"F4.wireOp",EDGE,"E22");Q1=makeQuery(id+"F6.boolean.opBoolean","SPLIT",EDGE,{"disambiguationData":[TD([makeQuery(id+"F1.opExtrude","SWEPT_FACE",FACE,{"disambiguationData":[OSD([sQuery(id+"F0.wireOp",EDGE,"E10.right")])]})])],"derivedFrom":makeQuery(id+"F6.opExtrude","SWEPT_EDGE",EDGE,{"disambiguationData":[OSD([subQ0,subQ2]),TDD([makeQuery(id+"F4.imprint","INTERSECT",VERTEX,{"disambiguationData":[OD(1.0)],"derivedFrom":[subQ0,subQ2]})])]})});}
            var Q2;
            Q2=makeQuery(id+"F6.opExtrude","CAP_EDGE",EDGE,{"disambiguationData":[OSD([sQuery(id+"F4.wireOp",EDGE,"E19")])],"isStart":false});
            var Q3;
            Q3=makeQuery(id+"F6.opExtrude","CAP_EDGE",EDGE,{"disambiguationData":[OSD([sQuery(id+"F4.wireOp",EDGE,"E22")])],"isStart":false});
            var Q4;
            Q4=makeQuery(id+"F6.opExtrude","CAP_EDGE",EDGE,{"disambiguationData":[OSD([sQuery(id+"F4.wireOp",EDGE,"E21")])],"isStart":true});
            var Q5;
            Q5=makeQuery(id+"F6.opExtrude","CAP_FACE",FACE,{"disambiguationData":[OSD([sQuery(id+"F4.wireOp",EDGE,"E19"),sQuery(id+"F4.wireOp",EDGE,"E21"),sQuery(id+"F4.wireOp",EDGE,"E22")])],"isStart":true});
            var Q6;
            {var subQ0=sQuery(id+"F4.wireOp",EDGE,"E19");var subQ2=sQuery(id+"F4.wireOp",EDGE,"E22");Q6=makeQuery(id+"F6.boolean.opBoolean","SPLIT",EDGE,{"disambiguationData":[TD([makeQuery(id+"F1.opExtrude","SWEPT_FACE",FACE,{"disambiguationData":[OSD([sQuery(id+"F0.wireOp",EDGE,"E10.right")])]})])],"derivedFrom":makeQuery(id+"F6.opExtrude","SWEPT_EDGE",EDGE,{"disambiguationData":[OSD([subQ0,subQ2]),TDD([makeQuery(id+"F4.imprint","INTERSECT",VERTEX,{"disambiguationData":[OD(0.0)],"derivedFrom":[subQ0,subQ2]})])]})});}
            var Q7;
            {var subQ0=sQuery(id+"F4.wireOp",EDGE,"E19");var subQ2=sQuery(id+"F4.wireOp",EDGE,"E22");Q7=makeQuery(id+"F6.boolean.opBoolean","SPLIT",EDGE,{"disambiguationData":[TD([makeQuery(id+"F1.opExtrude","SWEPT_FACE",FACE,{"disambiguationData":[OSD([sQuery(id+"F0.wireOp",EDGE,"E10.left")])]})])],"derivedFrom":makeQuery(id+"F6.opExtrude","SWEPT_EDGE",EDGE,{"disambiguationData":[OSD([subQ0,subQ2]),TDD([makeQuery(id+"F4.imprint","INTERSECT",VERTEX,{"disambiguationData":[OD(0.0)],"derivedFrom":[subQ0,subQ2]})])]})});}
            var Q8;
            {var subQ0=sQuery(id+"F4.wireOp",EDGE,"E19");var subQ2=sQuery(id+"F4.wireOp",EDGE,"E22");Q8=makeQuery(id+"F6.boolean.opBoolean","SPLIT",EDGE,{"disambiguationData":[TD([makeQuery(id+"F1.opExtrude","SWEPT_FACE",FACE,{"disambiguationData":[OSD([sQuery(id+"F0.wireOp",EDGE,"E10.left")])]})])],"derivedFrom":makeQuery(id+"F6.opExtrude","SWEPT_EDGE",EDGE,{"disambiguationData":[OSD([subQ0,subQ2]),TDD([makeQuery(id+"F4.imprint","INTERSECT",VERTEX,{"disambiguationData":[OD(1.0)],"derivedFrom":[subQ0,subQ2]})])]})});}
            var Q9;
            {var subQ0=sQuery(id+"F7.wireOp",EDGE,"E25");var subQ1=sQuery(id+"F0.wireOp",EDGE,"E10.left");Q9=makeQuery(id+"F8.boolean.opBoolean","COPY",EDGE,{"derivedFrom":makeQuery(id+"F8.opExtrude","CAP_EDGE",EDGE,{"disambiguationData":[OSD([subQ0]),TDD([makeQuery(id+"F7.imprint","IMPRINT",EDGE,{"disambiguationData":[TD([[makeQuery(id+"F7.imprint","INTERSECT",VERTEX,{"disambiguationData":[OD(0.0)],"derivedFrom":[makeQuery(id+"F1.opExtrude","SWEPT_EDGE",EDGE,{"disambiguationData":[OSD([sQuery(id+"F0.wireOp",EDGE,"E5"),sQuery(id+"F0.wireOp",EDGE,"E10.top"),subQ1])]}),subQ0]}),1.0]])],"derivedFrom":subQ0})])],"isStart":true})});}
            var Q10;
            {var subQ0=sQuery(id+"F7.wireOp",EDGE,"E25");var subQ1=sQuery(id+"F0.wireOp",EDGE,"E10.left");Q10=makeQuery(id+"F8.boolean.opBoolean","COPY",EDGE,{"derivedFrom":makeQuery(id+"F8.opExtrude","CAP_EDGE",EDGE,{"disambiguationData":[OSD([subQ0]),TDD([makeQuery(id+"F7.imprint","IMPRINT",EDGE,{"disambiguationData":[TD([[makeQuery(id+"F7.imprint","INTERSECT",VERTEX,{"disambiguationData":[OD(1.0)],"derivedFrom":[makeQuery(id+"F1.opExtrude","SWEPT_EDGE",EDGE,{"disambiguationData":[OSD([sQuery(id+"F0.wireOp",EDGE,"E5"),sQuery(id+"F0.wireOp",EDGE,"E10.top"),subQ1])]}),subQ0]}),-1.0]])],"derivedFrom":subQ0})])],"isStart":true})});}
            var Q11;
            {var subQ0=sQuery(id+"F7.wireOp",EDGE,"E25");var subQ1=sQuery(id+"F0.wireOp",EDGE,"E10.left");Q11=makeQuery(id+"F8.boolean.opBoolean","COPY",EDGE,{"derivedFrom":makeQuery(id+"F8.opExtrude","CAP_EDGE",EDGE,{"disambiguationData":[OSD([subQ0]),TDD([makeQuery(id+"F7.imprint","IMPRINT",EDGE,{"disambiguationData":[TD([[makeQuery(id+"F7.imprint","INTERSECT",VERTEX,{"disambiguationData":[OD(0.0)],"derivedFrom":[makeQuery(id+"F1.opExtrude","SWEPT_EDGE",EDGE,{"disambiguationData":[OSD([sQuery(id+"F0.wireOp",EDGE,"E5"),sQuery(id+"F0.wireOp",EDGE,"E10.top"),subQ1])]}),subQ0]}),1.0]])],"derivedFrom":subQ0})])],"isStart":false})});}
            var Q12;
            {var subQ0=sQuery(id+"F7.wireOp",EDGE,"E25");var subQ1=sQuery(id+"F0.wireOp",EDGE,"E10.left");Q12=makeQuery(id+"F8.boolean.opBoolean","COPY",EDGE,{"derivedFrom":makeQuery(id+"F8.opExtrude","CAP_EDGE",EDGE,{"disambiguationData":[OSD([subQ0]),TDD([makeQuery(id+"F7.imprint","IMPRINT",EDGE,{"disambiguationData":[TD([[makeQuery(id+"F7.imprint","INTERSECT",VERTEX,{"disambiguationData":[OD(1.0)],"derivedFrom":[makeQuery(id+"F1.opExtrude","SWEPT_EDGE",EDGE,{"disambiguationData":[OSD([sQuery(id+"F0.wireOp",EDGE,"E5"),sQuery(id+"F0.wireOp",EDGE,"E10.top"),subQ1])]}),subQ0]}),-1.0]])],"derivedFrom":subQ0})])],"isStart":false})});}
            fillet(context, id + "F10", {"entities" : qUnion([Q0, Q1, Q2, Q3, Q4, Q5, Q6, Q7, Q8, Q9, Q10, Q11, Q12]), "radius" : 5 * mm, "tangentPropagation" : true, "allowEdgeOverflow" : false});
        }
        {
            var Q0;
            Q0=makeQuery(id+"F9.opFillet","SPLIT",FACE,{"disambiguationData":[OD(0.0)],"derivedFrom":makeQuery(id+"F1.opExtrude","CAP_FACE",FACE,{"disambiguationData":[OSD([sQuery(id+"F0.wireOp",EDGE,"E0"),sQuery(id+"F0.wireOp",EDGE,"E1"),sQuery(id+"F0.wireOp",EDGE,"E2"),sQuery(id+"F0.wireOp",EDGE,"E3"),sQuery(id+"F0.wireOp",EDGE,"E4"),sQuery(id+"F0.wireOp",EDGE,"E5"),sQuery(id+"F0.wireOp",EDGE,"E6"),sQuery(id+"F0.wireOp",EDGE,"E7"),sQuery(id+"F0.wireOp",EDGE,"E8"),sQuery(id+"F0.wireOp",EDGE,"E10.bottom"),sQuery(id+"F0.wireOp",EDGE,"E10.left"),sQuery(id+"F0.wireOp",EDGE,"E10.right"),sQuery(id+"F0.wireOp",EDGE,"E12.bottom"),sQuery(id+"F0.wireOp",EDGE,"E12.left"),sQuery(id+"F0.wireOp",EDGE,"E12.right"),sQuery(id+"F0.wireOp",EDGE,"E13.bottom"),sQuery(id+"F0.wireOp",EDGE,"E13.left"),sQuery(id+"F0.wireOp",EDGE,"E13.right"),sQuery(id+"F0.wireOp",EDGE,"E14.left"),sQuery(id+"F0.wireOp",EDGE,"E14.right"),sQuery(id+"F0.wireOp",EDGE,"E15.left"),sQuery(id+"F0.wireOp",EDGE,"E15.right")])],"isStart":true})});
            var sketch = newSketch(context, id + "F11", { "sketchPlane" : qUnion([Q0])});
            skLineSegment(sketch, "E28", {"start": v(0, 15) * mm, "end": v(8, 31) * mm});
            skLineSegment(sketch, "E29", {"start": v(8, 31) * mm, "end": v(-8, 31) * mm});
            skLineSegment(sketch, "E30", {"start": v(-8, 31) * mm, "end": v(0, 15) * mm});
            skSolve(sketch);
        }
        {
            var Q0;
            Q0=qSketchRegion(id+"F11",true);
            extrude(context, id + "F12", {"entities" : qUnion([Q0]), "operationType" : NewBodyOperationType.REMOVE, "oppositeDirection" : true, "depth" : 400 * mm, "offsetDistance" : 25 * mm});
        }
    });
